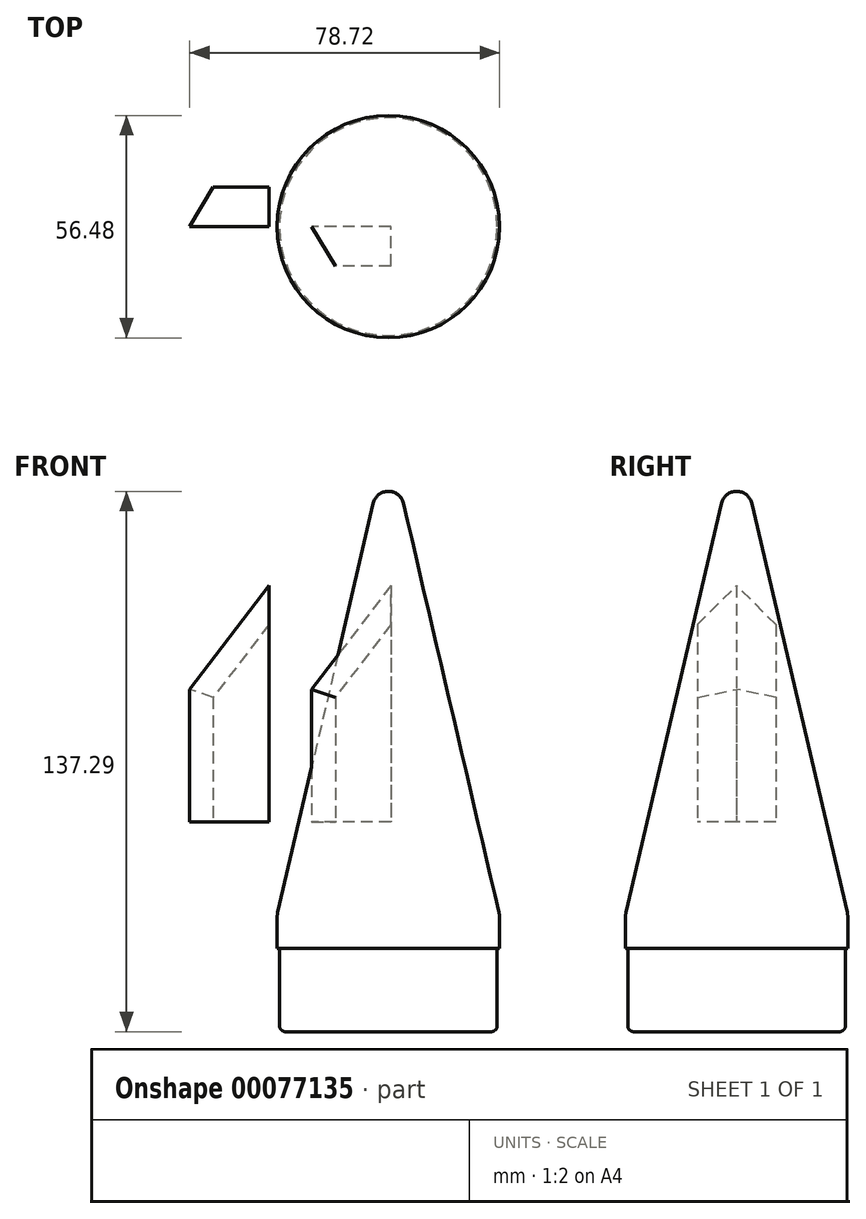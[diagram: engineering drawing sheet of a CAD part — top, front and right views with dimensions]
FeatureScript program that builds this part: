
annotation { "Feature Type Name" : "Feature", "Feature Type Description" : "" }
export const myFeature = defineFeature(function(context is Context, id is Id, definition is map)
    precondition{}
    {
        {
            var Q0;
            Q0=qCreatedBy(makeId("Front.planeOp"),FACE);
            var sketch = newSketch(context, id + "F0", { "sketchPlane" : qUnion([Q0])});
            skLineSegment(sketch, "E0", {"start": v(-33.3, -68.75) * mm, "end": v(-33.3, -68.75) * mm});
            skLineSegment(sketch, "E1", {"start": v(0, -68.75) * mm, "end": v(0, 58.15) * mm});
            skLineSegment(sketch, "E2", {"start": v(0, -68.75) * mm, "end": v(0, -78.75) * mm});
            skLineSegment(sketch, "E3", {"start": v(-32.6, -78.75) * mm, "end": v(-33.3, -78.75) * mm});
            skLineSegment(sketch, "E4", {"start": v(-33.3, -78.75) * mm, "end": v(-33.3, -68.75) * mm});
            skPoint(sketch, "E5.orphan", {"position": v(0, 61.25) * mm});
            skLineSegment(sketch, "E6", {"start": v(-33.3, -68.75) * mm, "end": v(-4.52, 54.56) * mm});
            skLineSegment(sketch, "E7.top", {"start": v(0, -103.75) * mm, "end": v(-32.6, -103.75) * mm});
            skLineSegment(sketch, "E7.left", {"start": v(0, -78.75) * mm, "end": v(0, -103.75) * mm});
            skLineSegment(sketch, "E7.right", {"start": v(-32.6, -78.75) * mm, "end": v(-32.6, -103.75) * mm});
            skArc(sketch, "E8", {"start": v(0, 58.15) * mm, "mid": v(-2.89, 57.15) * mm, "end": v(-4.52, 54.56) * mm});
            skSolve(sketch);
        }
        {
            var Q0;
            {var subQ0=sQuery(id+"F0.wireOp",EDGE,"E2");Q0=makeQuery(id+"F0.imprint","IMPRINT",FACE,{"disambiguationData":[TD([[makeQuery(id+"F0.imprint","IMPRINT",EDGE,{"derivedFrom":subQ0}),-1.0]])]});}
            var Q1;
            Q1=sQuery(id+"F0.wireOp",EDGE,"E1");
            revolve(context, id + "F1", {"entities" : qUnion([Q0]), "axis" : qUnion([Q1]), "revolveType" : RevolveType.FULL});
        }
        {
            var Q0;
            Q0=makeQuery(id+"F1.opRevolve","SWEPT_BODY",BODY,{"disambiguationData":[OSD([sQuery(id+"F0.wireOp",EDGE,"Oh61cgLR-RQo2-T4aV-TcRg-Gp7ijPdUG9jl"),sQuery(id+"F0.wireOp",EDGE,"E1"),sQuery(id+"F0.wireOp",EDGE,"E2"),sQuery(id+"F0.wireOp",EDGE,"E3"),sQuery(id+"F0.wireOp",EDGE,"E4"),sQuery(id+"F0.wireOp",EDGE,"E0"),sQuery(id+"F0.wireOp",EDGE,"dTV1AxgJ-VMAe-DLQO-Zqz3-4UbtDb8FiUJC")])]});
            var Q1;
            Q1=qCreatedBy(makeId("Origin.pointOp"),VERTEX);
            transform(context, id + "F2", {"entities" : qUnion([Q0]), "transformType" : TransformType.SCALE_UNIFORMLY, "scale" : .848, "scalePoint" : qUnion([Q1]), "makeCopy" : false});
        }
        {
            var Q0;
            Q0=qCreatedBy(makeId("Front.planeOp"),FACE);
            var sketch = newSketch(context, id + "F3", { "sketchPlane" : qUnion([Q0])});
            skLineSegment(sketch, "E9", {"start": v(-53.48, -34.72) * mm, "end": v(-53.48, 0) * mm});
            skLineSegment(sketch, "E10", {"start": v(-53.48, 0) * mm, "end": v(-30.36, 30.27) * mm});
            skLineSegment(sketch, "E11", {"start": v(-30.36, 30.27) * mm, "end": v(-30.36, -34.72) * mm});
            skLineSegment(sketch, "E12", {"start": v(-30.36, -34.72) * mm, "end": v(-53.48, -34.72) * mm});
            skSolve(sketch);
        }
        {
            var Q0;
            Q0=makeQuery(id+"F3.imprint","IMPRINT",FACE,{"disambiguationData":[TD([[makeQuery(id+"F3.imprint","IMPRINT",EDGE,{"derivedFrom":sQuery(id+"F3.wireOp",EDGE,"E9")}),-1.0]])]});
            extrude(context, id + "F4", {"entities" : qUnion([Q0]), "depth" : 10 * mm, "offsetDistance" : 25 * mm});
        }
        {
            var Q0;
            Q0=makeQuery(id+"F4.opExtrude","CAP_EDGE",EDGE,{"disambiguationData":[OSD([sQuery(id+"F3.wireOp",EDGE,"E10")])],"isStart":false});
            var Q1;
            Q1=makeQuery(id+"F4.opExtrude","CAP_EDGE",EDGE,{"disambiguationData":[OSD([sQuery(id+"F3.wireOp",EDGE,"E9")])],"isStart":false});
            chamfer(context, id + "F5", {"entities" : qUnion([Q0, Q1]), "chamferType" : ChamferType.TWO_OFFSETS, "width1" : 9 * mm, "oppositeDirection" : false, "width2" : 15 * mm, "tangentPropagation" : true});
        }
        {
            var Q0;
            Q0=makeQuery(id+"F4.opExtrude","SWEPT_BODY",BODY,{"disambiguationData":[OSD([sQuery(id+"F3.wireOp",EDGE,"E9"),sQuery(id+"F3.wireOp",EDGE,"E10"),sQuery(id+"F3.wireOp",EDGE,"E11"),sQuery(id+"F3.wireOp",EDGE,"E12")])]});
            var Q1;
            Q1=qCreatedBy(makeId("Front.planeOp"),FACE);
            mirror(context, id + "F6", {"operationType" : NewBodyOperationType.ADD, "entities" : qUnion([Q0]), "mirrorPlane" : qUnion([Q1])});
        }
        {
            var Q0;
            Q0=makeQuery(id+"F4.opExtrude","SWEPT_BODY",BODY,{"disambiguationData":[OSD([sQuery(id+"F3.wireOp",EDGE,"E9"),sQuery(id+"F3.wireOp",EDGE,"E10"),sQuery(id+"F3.wireOp",EDGE,"E11"),sQuery(id+"F3.wireOp",EDGE,"E12")])]});
            transform(context, id + "F7", {"entities" : qUnion([Q0]), "transformType" : TransformType.TRANSLATION_3D, "dx" : 31 * mm, "dy" : 0 * mm, "dz" : 0 * mm, "makeCopy" : false});
        }
        {
            var Q0;
            Q0=makeQuery(id+"F1.opRevolve","SWEPT_EDGE",EDGE,{"disambiguationData":[OSD([sQuery(id+"F0.wireOp",EDGE,"E4"),sQuery(id+"F0.wireOp",EDGE,"E6")])]});
            fillet(context, id + "F8", {"entities" : qUnion([Q0]), "radius" : 5 * mm, "tangentPropagation" : true, "allowEdgeOverflow" : false});
        }
        {
            var Q0;
            Q0=makeQuery(id+"F1.opRevolve","SWEPT_EDGE",EDGE,{"disambiguationData":[OSD([sQuery(id+"F0.wireOp",EDGE,"E7.top"),sQuery(id+"F0.wireOp",EDGE,"E7.right")])]});
            fillet(context, id + "F9", {"entities" : qUnion([Q0]), "radius" : 1.5 * mm, "tangentPropagation" : true, "allowEdgeOverflow" : false});
        }
    });
